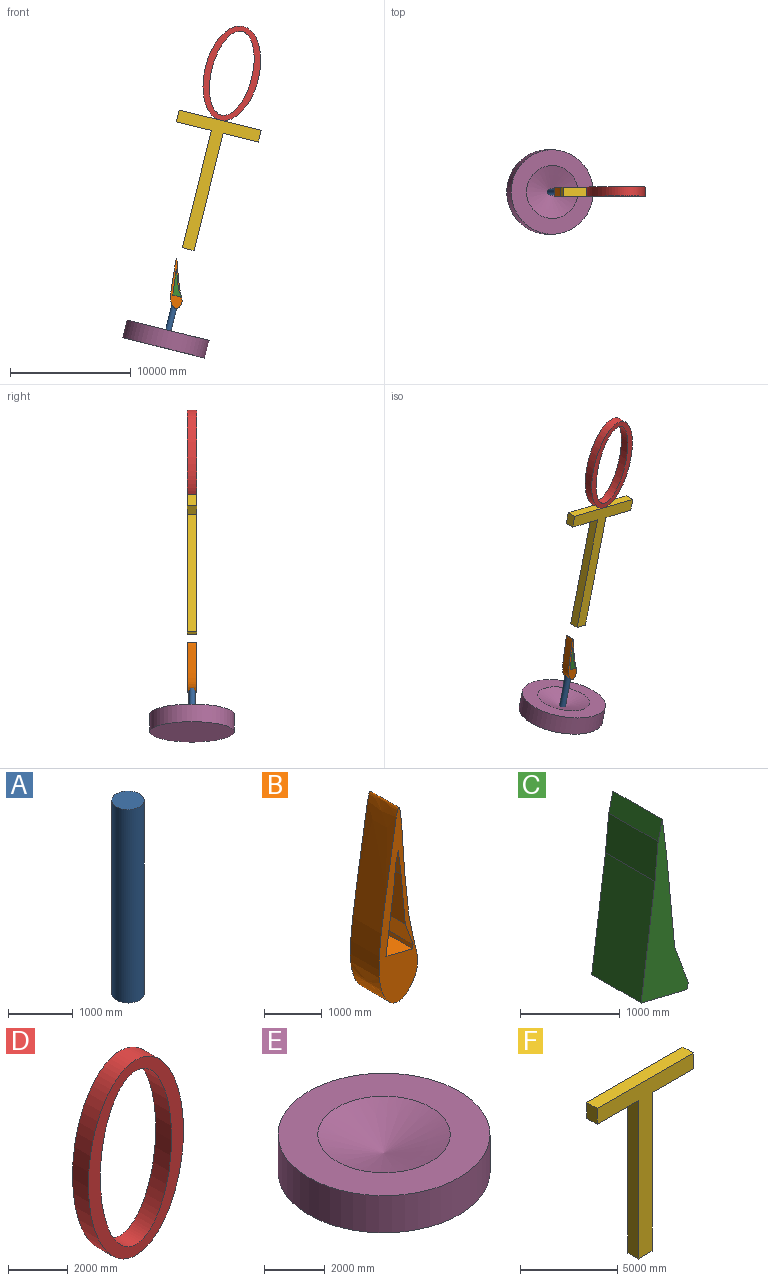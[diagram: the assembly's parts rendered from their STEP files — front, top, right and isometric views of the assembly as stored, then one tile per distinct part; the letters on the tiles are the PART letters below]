
ASSEMBLY  parts=6 mates=5
PART A: 3 faces, bbox 500x500x3670 mm
  f0: cylinder r=250mm len=3670mm, axis (0,0,-1), area 5764822.5mm2, adj f1,f2
  f1: plane 500x500mm, normal (0,0,1), area 196349.5mm2, adj f0
  f2: plane 500x500mm, normal (0,0,-1), area 196349.5mm2, adj f0
PART B: 12 faces, bbox 1215.2x700x4374.6 mm
  f0: plane 700x80.05mm, normal (-0.97,0,0.24), area 57730.5mm2, adj f1,f4,f5,f11
  f1: plane 700x646.55mm, normal (0.24,0,0.97), area 466256.6mm2, adj f0,f4,f5,f6
  f2: cylinder r=430.09mm len=700mm, axis (0,1,0), area 62106.4mm2, adj f3,f4,f5
  f3: extruded ~4091.56x943.62mm, area 6093494.4mm2, adj f2,f4,f5
  f4: plane 4374.65x1215.21mm, normal (0,-1,0), area 1546226mm2, adj f0,f1,f2,f3,f6,f7,f8,f9
  f5: plane 4374.65x1215.21mm, normal (0,1,0), area 1546226mm2, adj f0,f1,f2,f3,f6,f7,f8,f9
  f6: plane 1396.43x700mm, normal (0.99,0,-0.14), area 986949.4mm2, adj f1,f4,f5,f7
  f7: plane 700x462.71mm, normal (1,0,-0.1), area 325437.8mm2, adj f4,f5,f6,f8
  f8: plane 700x240.66mm, normal (0.97,0,-0.24), area 173552.2mm2, adj f4,f5,f7,f9
  f9: plane 700x530.57mm, normal (-0.99,0,-0.13), area 374397.4mm2, adj f4,f5,f8,f10
  f10: plane 1124.03x700mm, normal (-1,0,-0.09), area 790364.6mm2, adj f4,f5,f9,f11
  f11: plane 700x525.25mm, normal (-0.94,0,-0.34), area 391607.1mm2, adj f0,f4,f5,f10
PART C: 10 faces, bbox 666.4x700x2259.9 mm
  f0: plane 1396.43x700mm, normal (-0.99,0,0.14), area 986949.4mm2, adj f1,f7,f8,f9
  f1: plane 700x646.55mm, normal (-0.24,0,-0.97), area 466256.6mm2, adj f0,f2,f8,f9
  f2: plane 700x80.05mm, normal (0.97,0,-0.24), area 57730.5mm2, adj f1,f3,f8,f9
  f3: plane 700x525.25mm, normal (0.94,0,0.34), area 391607.1mm2, adj f2,f4,f8,f9
  f4: plane 1124.03x700mm, normal (1,0,0.09), area 790364.6mm2, adj f3,f5,f8,f9
  f5: plane 700x530.57mm, normal (0.99,0,0.13), area 374397.4mm2, adj f4,f6,f8,f9
  f6: plane 700x240.66mm, normal (-0.97,0,0.24), area 173552.2mm2, adj f5,f7,f8,f9
  f7: plane 700x462.71mm, normal (-1,0,0.1), area 325437.8mm2, adj f0,f6,f8,f9
  f8: plane 2259.91x666.38mm, normal (0,-1,0), area 648285.8mm2, adj f0,f1,f2,f3,f4,f5,f6,f7
  f9: plane 2259.91x666.38mm, normal (0,1,0), area 648285.8mm2, adj f0,f1,f2,f3,f4,f5,f6,f7
PART D: 4 faces, bbox 4500x750x8000 mm
  f0: extruded ~7125x3375mm, area 12768333mm2, adj f2,f3
  f1: extruded ~8000x4500mm, area 15016475.7mm2, adj f2,f3
  f2: plane 8000x4500mm, normal (0,-1,0), area 9387962.4mm2, adj f0,f1
  f3: plane 8000x4500mm, normal (0,1,0), area 9387962.4mm2, adj f0,f1
PART E: 4 faces, bbox 7000x7000x1500 mm
  f0: cone r=2187.5mm half-angle=71.1deg, axis (0,0,1), area 15892041mm2, adj f1
  f1: plane 7000x7000mm, normal (0,0,1), area 23451498.3mm2, adj f0,f2
  f2: cylinder r=3500mm len=7000mm, axis (0,0,-1), area 32986722.9mm2, adj f1,f3
  f3: plane 7000x7000mm, normal (0,0,-1), area 38484510mm2, adj f2
PART F: 10 faces, bbox 7000x750x11000 mm
  f0: plane 7000x750mm, normal (0,0,1), area 5250000mm2, adj f1,f7,f8,f9
  f1: plane 1000x750mm, normal (-1,0,0), area 750000mm2, adj f0,f2,f8,f9
  f2: plane 3000x750mm, normal (0,0,-1), area 2250000mm2, adj f1,f3,f8,f9
  f3: plane 10000x750mm, normal (-1,0,0), area 7500000mm2, adj f2,f4,f8,f9
  f4: plane 1000x750mm, normal (0,0,-1), area 750000mm2, adj f3,f5,f8,f9
  f5: plane 10000x750mm, normal (1,0,0), area 7500000mm2, adj f4,f6,f8,f9
  f6: plane 3000x750mm, normal (0,0,-1), area 2250000mm2, adj f5,f7,f8,f9
  f7: plane 1000x750mm, normal (1,0,0), area 750000mm2, adj f0,f6,f8,f9
  f8: plane 11000x7000mm, normal (0,-1,0), area 17000000mm2, adj f0,f1,f2,f3,f4,f5,f6,f7
  f9: plane 11000x7000mm, normal (0,1,0), area 17000000mm2, adj f0,f1,f2,f3,f4,f5,f6,f7
PLACE A rot(axis=(0,1,0),13.9deg) t=(1918.89,2677.55,-2260.14)mm
PLACE B t=(2960.48,2677.55,-2127.56)mm
PLACE C t=(2960.48,2677.55,-2127.56)mm
PLACE D rot(axis=(0.99,0,-0.12),180deg) t=(10964.75,2302.55,32188.9)mm
PLACE E rot(axis=(0,1,0),13.9deg) t=(1899.67,2677.55,-2337.79)mm
PLACE F rot(axis=(0,1,0),13.9deg) t=(5064.35,3052.55,8361.82)mm
MATE fastened F.f4 <-> A.f0  axis (-0.24,0,-0.97) through (3923.61,2677.55,5835.34)mm
MATE fastened D.f3 <-> F.f8  axis (0,-1,0) through (7529.21,2302.55,20395.55)mm
MATE fastened A.f0 <-> C.f1  axis (0.24,0,0.97) through (2962.12,2677.55,1952.62)mm
MATE fastened A.f0 <-> E.f0  axis (-0.24,0,-0.97) through (2079.95,2677.55,-1609.78)mm
MATE fastened B.f1 <-> A.f0  axis (0.24,0,0.97) through (2962.12,2677.55,1952.62)mm
